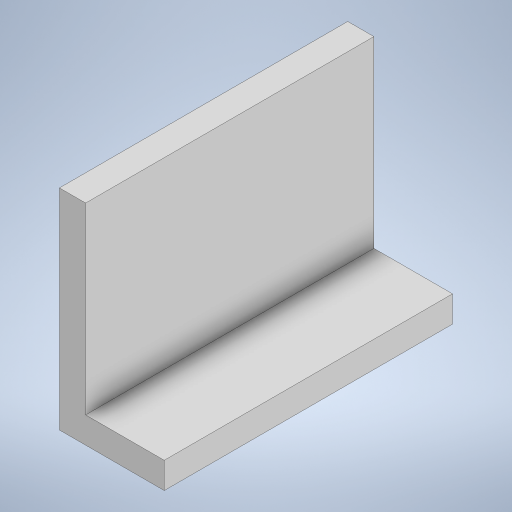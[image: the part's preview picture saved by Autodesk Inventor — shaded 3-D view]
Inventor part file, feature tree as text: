
AUTODESK INVENTOR PART (.ipt)
format: ipt  version: 2023 (Build 270158000, 158)  size: 195,584 bytes
history: native  units: in
note: dims shown in document units (in); Inventor stores cm internally (conversion verified against a paired STEP export)
features: extrude x1, sketch x1
ambient origin geometry x8: Origin, YZ Plane, XZ Plane, XY Plane, X Axis, Y Axis, Z Axis, Center Point
bodies: Solid1 (feature_tree)
feature tree (2):
  extrude  "Extrusion1"  Depth=0.6299in
  sketch  "Sketch1"  dims[d0=0.0787in d1=0.6299in d2=0.2362in d3=0.8661in d4=0.0in]
